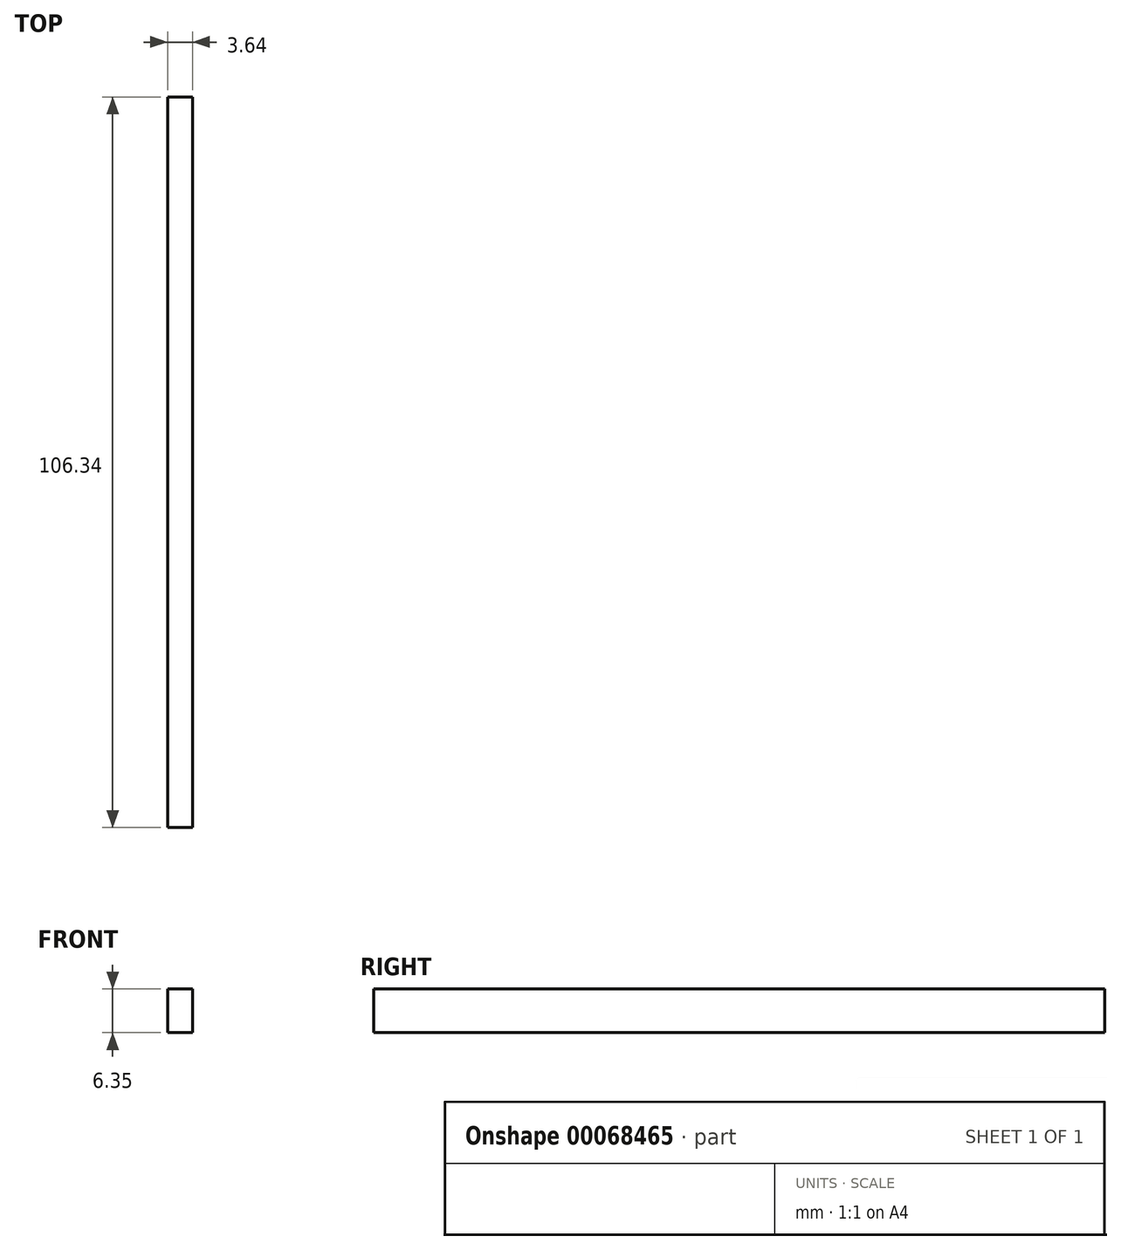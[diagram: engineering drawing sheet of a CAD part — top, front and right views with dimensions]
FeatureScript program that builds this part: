
annotation { "Feature Type Name" : "Feature", "Feature Type Description" : "" }
export const myFeature = defineFeature(function(context is Context, id is Id, definition is map)
    precondition{}
    {
        {
            var Q0;
            Q0=qCreatedBy(makeId("Top.planeOp"),FACE);
            var sketch = newSketch(context, id + "F0", { "sketchPlane" : qUnion([Q0])});
            skLineSegment(sketch, "E0.rect.bottom", {"start": v(-1.82, 53.17) * mm, "end": v(1.83, 53.17) * mm});
            skLineSegment(sketch, "E0.rect.top", {"start": v(-1.83, -53.17) * mm, "end": v(1.82, -53.17) * mm});
            skLineSegment(sketch, "E0.rect.left", {"start": v(-1.82, 53.17) * mm, "end": v(-1.83, -53.17) * mm});
            skLineSegment(sketch, "E0.rect.right", {"start": v(1.83, 53.17) * mm, "end": v(1.82, -53.17) * mm});
            skPoint(sketch, "E0.rect.middle", {"position": v(0, 0) * mm});
            skSolve(sketch);
        }
        {
            var Q0;
            Q0=makeQuery(id+"F0.imprint","IMPRINT",FACE,{"disambiguationData":[TD([[makeQuery(id+"F0.imprint","IMPRINT",EDGE,{"derivedFrom":sQuery(id+"F0.wireOp",EDGE,"E0.rect.bottom")}),-1.0]])]});
            extrude(context, id + "F1", {"entities" : qUnion([Q0]), "depth" : 6.35 * mm});
        }
    });
